# Revit family: Washbasin-GBG-Nautic_Bolt_Mounting
name_source: partatom
category: Plumbing Fixtures
units: mm (PartAtom-declared; Revit-internal decimal feet)

## family parameters
Cut with Voids When Loaded = No
Host = Face
OmniClass Number = 23.45.05.14.14
OmniClass Title = Sinks/Lavatories
Part Type = Normal
Room Calculation Point = No
Round Connector Dimension = Use Radius
Shared = No

## types (1)
- With Mixer Hole to Right
    Article Number = 5540 9R 01
    Assembly Code = D2010400
    BIMobject category = Basins
    CW Connection = Yes
    Care Instruction URL = http://www.gustavsberg.com
    Code EAN = 4047289973362
    Code LVI FIN = 5613011
    Code NRF NOR = 6020201
    Code RSK SWE = 7455050
    Code VVS DNK = 626250200
    Default Elevation = 850 mm
    Description = 5540 Nautic washbasin for bolt mounting
    Design country = Sweden
    EAN code = https://4047289973362
    Edition number = 1
    Height = 175 mm
    Installation Instruction URL = http://www.gustavsberg.com
    Installation instructions = http://www.gustavsberg.com
    L Mixer Hole = No
    Length = 275 mm
    Manufacturer = Villeroy & Boch Gustavsberg AB
    Manufacturer country = Hungary
    Manufacturer name = Gustavsberg
    Material = Gustavsberg Porcelain - White
    Material main = Porcelain
    Model = 5540
    Mounting Height = 850 mm
    Nominal height = 0
    Nominal width = 0
    Product Guid = d1d711f7-6196-4ef9-b3fc-618ff4a330c2
    Product Page URL = http://www.gustavsberg.com
    Product SKU = 5540
    Product certification = http://www.gustavsberg.com
    Product data url = https://bimobject.com
    Product group = Washbasin
    QR code = http://bimobject.com
    R Mixer Hole = Yes
    Type Comments = 5540 with mixer hole to right
    URL = http://www.gustavsberg.com
    Waste Connection = Yes
    Waste Connection Diameter = 50 mm  [stored 0.164042 ft]
    Waste Connection Radius = 25 mm  [stored 0.082021 ft]
    Weight Net (Kg) = 0
    Width = 400 mm

note: [stored X ft] marks values corroborated as IEEE doubles in the binary element streams (Revit-internal decimal feet)

## geometry (parser evidence)
native form markers: Blend x4, Sweep x1
no freeform markers — native parametric forms only
